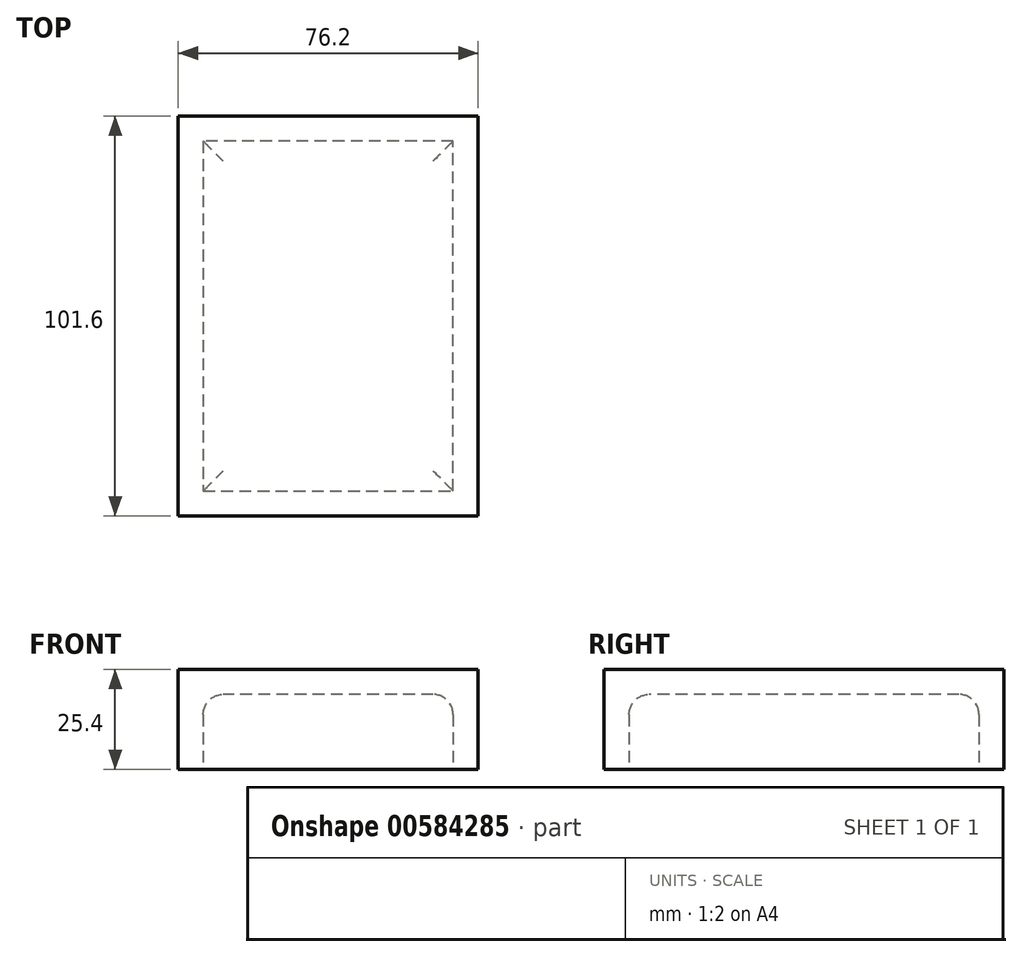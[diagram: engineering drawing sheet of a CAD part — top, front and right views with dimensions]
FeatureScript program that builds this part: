
annotation { "Feature Type Name" : "Feature", "Feature Type Description" : "" }
export const myFeature = defineFeature(function(context is Context, id is Id, definition is map)
    precondition{}
    {
        {
            var Q0;
            Q0=qCreatedBy(makeId("Top.planeOp"),FACE);
            var sketch = newSketch(context, id + "F0", { "sketchPlane" : qUnion([Q0])});
            skLineSegment(sketch, "E0.bottom", {"start": v(38.1, 50.8) * mm, "end": v(-38.1, 50.8) * mm});
            skLineSegment(sketch, "E0.top", {"start": v(38.1, -50.8) * mm, "end": v(-38.1, -50.8) * mm});
            skLineSegment(sketch, "E0.left", {"start": v(38.1, 50.8) * mm, "end": v(38.1, -50.8) * mm});
            skLineSegment(sketch, "E0.right", {"start": v(-38.1, 50.8) * mm, "end": v(-38.1, -50.8) * mm});
            skPoint(sketch, "E0.middle", {"position": v(0, 0) * mm});
            skSolve(sketch);
        }
        {
            var Q0;
            Q0=qCreatedBy(makeId("Top.planeOp"),FACE);
            var sketch = newSketch(context, id + "F1", { "sketchPlane" : qUnion([Q0])});
            skLineSegment(sketch, "E1.0", {"start": v(-31.75, -44.45) * mm, "end": v(31.75, -44.45) * mm});
            skLineSegment(sketch, "E1.1", {"start": v(-31.75, 44.45) * mm, "end": v(-31.75, -44.45) * mm});
            skLineSegment(sketch, "E1.2", {"start": v(31.75, 44.45) * mm, "end": v(-31.75, 44.45) * mm});
            skLineSegment(sketch, "E1.3", {"start": v(31.75, -44.45) * mm, "end": v(31.75, 44.45) * mm});
            skSolve(sketch);
        }
        {
            var Q0;
            Q0 = qSketchRegion(id + "F0", true);
            extrude(context, id + "F2", {"entities" : qUnion([Q0]), "depth" : 25.4 * mm, "offsetDistance" : 25.4 * mm});
        }
        {
            var Q0;
            Q0 = qSketchRegion(id + "F1", true);
            extrude(context, id + "F3", {"entities" : qUnion([Q0]), "depth" : 19.05 * mm, "offsetDistance" : 25.4 * mm});
        }
        {
            var Q0;
            Q0=makeQuery(id+"F3.opExtrude","CAP_EDGE",EDGE,{"disambiguationData":[OSD([sQuery(id+"F1.wireOp",EDGE,"E1.0")])],"isStart":false});
            var Q1;
            Q1=makeQuery(id+"F3.opExtrude","CAP_EDGE",EDGE,{"disambiguationData":[OSD([sQuery(id+"F1.wireOp",EDGE,"E1.3")])],"isStart":false});
            var Q2;
            Q2=makeQuery(id+"F3.opExtrude","CAP_EDGE",EDGE,{"disambiguationData":[OSD([sQuery(id+"F1.wireOp",EDGE,"E1.2")])],"isStart":false});
            var Q3;
            Q3=makeQuery(id+"F3.opExtrude","CAP_EDGE",EDGE,{"disambiguationData":[OSD([sQuery(id+"F1.wireOp",EDGE,"E1.1")])],"isStart":false});
            fillet(context, id + "F4", {"entities" : qUnion([Q0, Q1, Q2, Q3]), "radius" : 5.08 * mm, "tangentPropagation" : true, "allowEdgeOverflow" : false});
        }
    });
